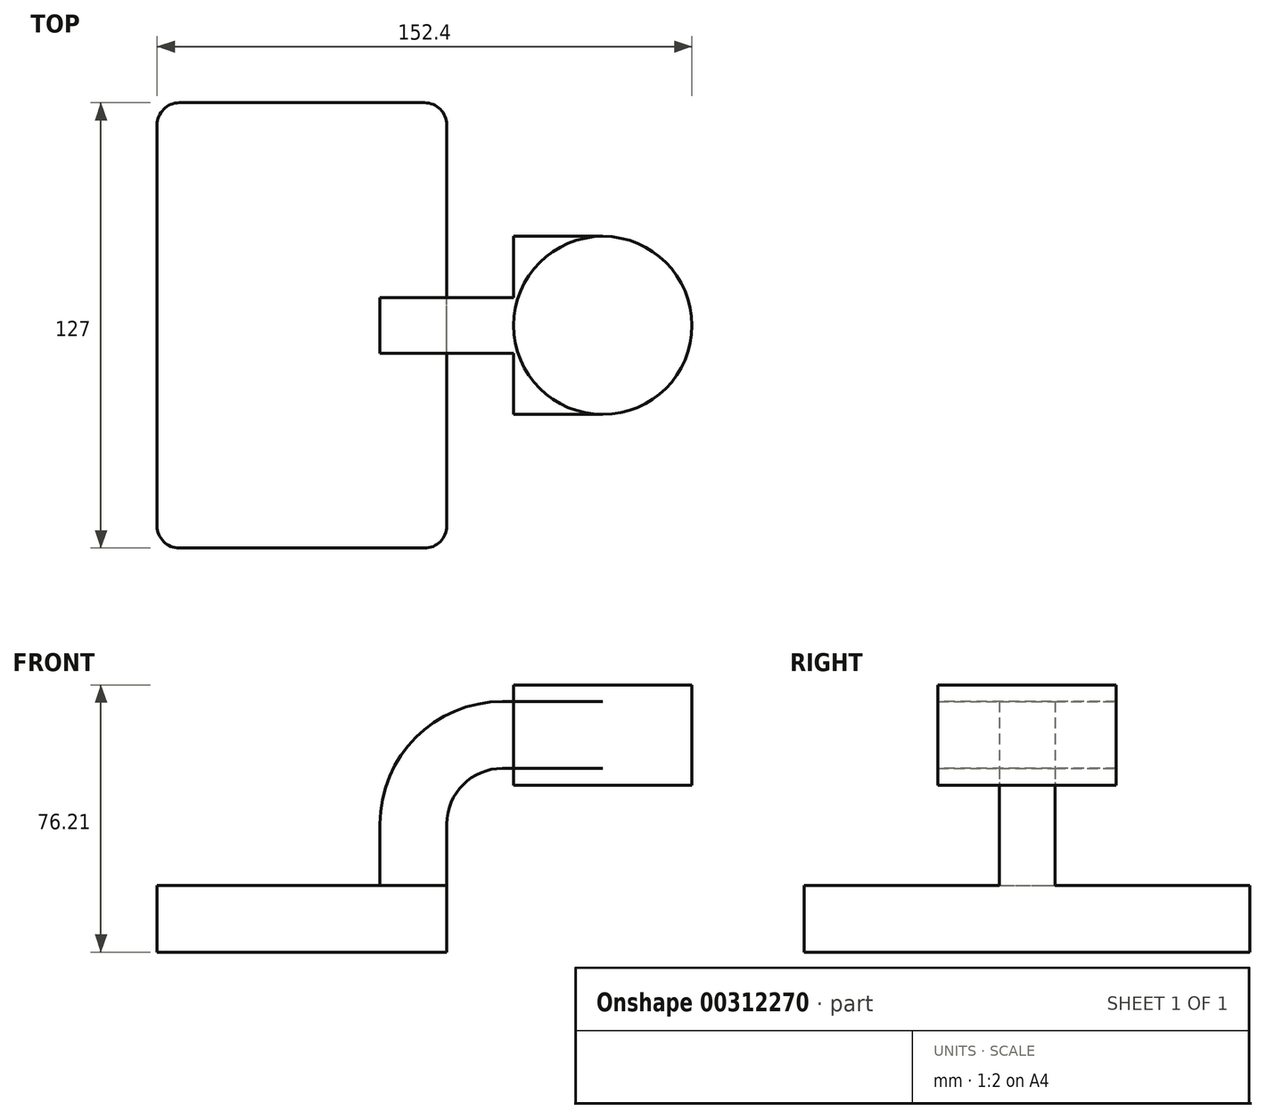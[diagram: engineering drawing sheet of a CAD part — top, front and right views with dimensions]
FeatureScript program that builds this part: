
annotation { "Feature Type Name" : "Feature", "Feature Type Description" : "" }
export const myFeature = defineFeature(function(context is Context, id is Id, definition is map)
    precondition{}
    {
        {
            var Q0;
            Q0=qCreatedBy(makeId("Front.planeOp"),FACE);
            var sketch = newSketch(context, id + "F0", { "sketchPlane" : qUnion([Q0])});
            skLineSegment(sketch, "E0.bottom", {"start": v(41.27, 9.53) * mm, "end": v(-41.28, 9.53) * mm});
            skLineSegment(sketch, "E0.top", {"start": v(41.28, -9.52) * mm, "end": v(-41.27, -9.52) * mm});
            skLineSegment(sketch, "E0.left", {"start": v(41.28, 9.53) * mm, "end": v(41.28, -9.52) * mm});
            skLineSegment(sketch, "E0.right", {"start": v(-41.28, 9.53) * mm, "end": v(-41.27, -9.52) * mm});
            skPoint(sketch, "E0.middle", {"position": v(0, 0) * mm});
            skLineSegment(sketch, "E1.bottom", {"start": v(111.12, 66.68) * mm, "end": v(60.32, 66.68) * mm});
            skLineSegment(sketch, "E1.top", {"start": v(111.12, 38.1) * mm, "end": v(60.32, 38.1) * mm});
            skLineSegment(sketch, "E1.left", {"start": v(111.12, 66.68) * mm, "end": v(111.13, 38.1) * mm});
            skLineSegment(sketch, "E1.right", {"start": v(60.32, 66.68) * mm, "end": v(60.32, 38.1) * mm});
            skPoint(sketch, "E1.middle", {"position": v(85.72, 52.39) * mm});
            skArc(sketch, "E2", {"start": v(41.27, 27) * mm, "mid": v(45.92, 38.23) * mm, "end": v(57.15, 42.88) * mm});
            skLineSegment(sketch, "E3", {"start": v(57.15, 42.88) * mm, "end": v(85.72, 42.88) * mm});
            skArc(sketch, "E4.1", {"start": v(22.22, 27) * mm, "mid": v(32.45, 51.7) * mm, "end": v(57.15, 61.93) * mm});
            skLineSegment(sketch, "E4.2", {"start": v(22.22, 9.53) * mm, "end": v(22.22, 27) * mm});
            skLineSegment(sketch, "E5", {"start": v(41.27, 27) * mm, "end": v(41.27, 8.73) * mm});
            skLineSegment(sketch, "E6", {"start": v(85.72, 66.68) * mm, "end": v(85.72, 38.1) * mm});
            skFitSpline(sketch, "E7", {"points": [v(-41.28, 9.53) * mm, v(57.15, 61.93) * mm], "startDerivative": vector(161.92, 79.98) * mm, "endDerivative": vector(129.69, -2.12) * mm});
            skLineSegment(sketch, "E8", {"start": v(57.15, 61.93) * mm, "end": v(85.72, 61.93) * mm});
            skSolve(sketch);
        }
        {
            var Q0;
            Q0=makeQuery(id+"F0.imprint","IMPRINT",FACE,{"disambiguationData":[TD([[makeQuery(id+"F0.imprint","IMPRINT",EDGE,{"derivedFrom":sQuery(id+"F0.wireOp",EDGE,"E0.top")}),-1.0]])]});
            extrude(context, id + "F1", {"entities" : qUnion([Q0]), "endBound" : BoundingType.SYMMETRIC, "depth" : 127 * mm});
        }
        {
            var Q0;
            {var subQ1=sQuery(id+"F0.wireOp",EDGE,"E2");Q0=makeQuery(id+"F0.imprint","IMPRINT",FACE,{"disambiguationData":[TD([[makeQuery(id+"F0.imprint","IMPRINT",EDGE,{"derivedFrom":subQ1}),1.0]])]});}
            var Q1;
            {var subQ0=sQuery(id+"F0.wireOp",EDGE,"E8");var subQ1=sQuery(id+"F0.wireOp",EDGE,"E1.right");var subQ2=makeQuery(id+"F0.imprint","INTERSECT",VERTEX,{"derivedFrom":[subQ1,subQ0]});Q1=makeQuery(id+"F0.imprint","IMPRINT",FACE,{"disambiguationData":[TD([[makeQuery(id+"F0.imprint","IMPRINT",EDGE,{"disambiguationData":[TD([[subQ2,-1.0]])],"derivedFrom":subQ1}),1.0]])]});}
            extrude(context, id + "F2", {"entities" : qUnion([Q0, Q1]), "operationType" : NewBodyOperationType.ADD, "endBound" : BoundingType.SYMMETRIC, "depth" : 50.8 * mm});
        }
        {
            var Q0;
            Q0=makeQuery(id+"F0.imprint","IMPRINT",FACE,{"disambiguationData":[TD([[makeQuery(id+"F0.imprint","IMPRINT",EDGE,{"derivedFrom":sQuery(id+"F0.wireOp",EDGE,"E4.1")}),1.0]])]});
            extrude(context, id + "F3", {"entities" : qUnion([Q0]), "operationType" : NewBodyOperationType.ADD, "endBound" : BoundingType.SYMMETRIC, "depth" : 15.88 * mm});
        }
        {
            var Q0;
            {var subQ0=sQuery(id+"F0.wireOp",EDGE,"E1.left");Q0=makeQuery(id+"F0.imprint","IMPRINT",FACE,{"disambiguationData":[TD([[makeQuery(id+"F0.imprint","IMPRINT",EDGE,{"derivedFrom":subQ0}),-1.0]])]});}
            var Q1;
            Q1=sQuery(id+"F0.wireOp",EDGE,"E6");
            revolve(context, id + "F4", {"operationType" : NewBodyOperationType.ADD, "entities" : qUnion([Q0]), "axis" : qUnion([Q1]), "revolveType" : RevolveType.FULL});
        }
        {
            var Q0;
            Q0=makeQuery(id+"F1.opExtrude","CAP_EDGE",EDGE,{"disambiguationData":[OSD([sQuery(id+"F0.wireOp",EDGE,"E0.left"),sQuery(id+"F0.wireOp",EDGE,"E5")])],"isStart":false});
            var Q1;
            Q1=makeQuery(id+"F1.opExtrude","CAP_EDGE",EDGE,{"disambiguationData":[OSD([sQuery(id+"F0.wireOp",EDGE,"E0.right")])],"isStart":false});
            var Q2;
            Q2=makeQuery(id+"F1.opExtrude","CAP_EDGE",EDGE,{"disambiguationData":[OSD([sQuery(id+"F0.wireOp",EDGE,"E0.right")])],"isStart":true});
            var Q3;
            Q3=makeQuery(id+"F1.opExtrude","CAP_EDGE",EDGE,{"disambiguationData":[OSD([sQuery(id+"F0.wireOp",EDGE,"E0.left"),sQuery(id+"F0.wireOp",EDGE,"E5")])],"isStart":true});
            fillet(context, id + "F5", {"entities" : qUnion([Q0, Q1, Q2, Q3]), "radius" : 6.35 * mm, "tangentPropagation" : true, "allowEdgeOverflow" : false});
        }
    });
